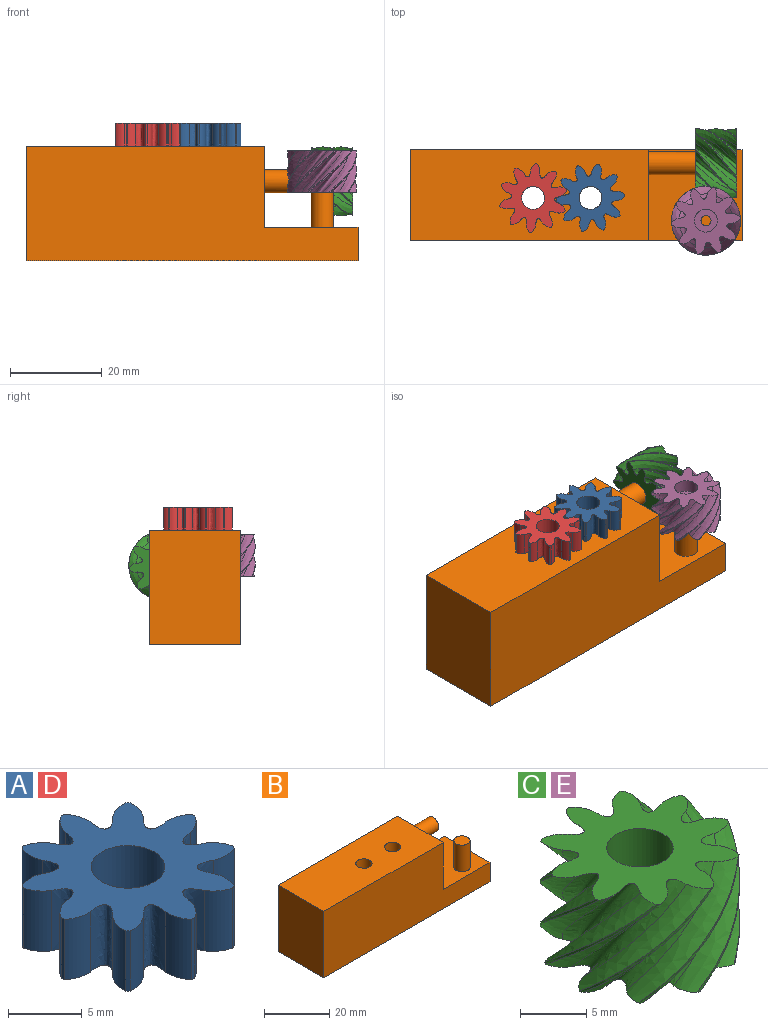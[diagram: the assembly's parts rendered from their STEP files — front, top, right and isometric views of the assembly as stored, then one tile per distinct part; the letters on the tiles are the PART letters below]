
ASSEMBLY  parts=5 mates=4
PART A: 43 faces, bbox 14.9x14.9x5 mm
  f0: cylinder r=2.5mm len=5mm, axis (0,0,-1), area 9.9mm2, adj f1,f39,f40,f41
  f1: cylinder r=7.5mm len=5mm, axis (0,0,-1), area 1.6mm2, adj f0,f2,f40,f41
  f2: cylinder r=2.5mm len=5mm, axis (0,0,-1), area 9.9mm2, adj f1,f3,f40,f41
  f3: extruded ~5x1.49mm, area 14.6mm2, adj f2,f4,f40,f41
  f4: cylinder r=2.5mm len=5mm, axis (0,0,-1), area 9.9mm2, adj f3,f5,f40,f41
  f5: cylinder r=7.5mm len=5mm, axis (0,0,-1), area 1.6mm2, adj f4,f6,f40,f41
  f6: cylinder r=2.5mm len=5mm, axis (0,0,-1), area 9.9mm2, adj f5,f7,f40,f41
  f7: extruded ~5x1.49mm, area 14.6mm2, adj f6,f8,f40,f41
  f8: cylinder r=2.5mm len=5mm, axis (0,0,-1), area 9.9mm2, adj f7,f9,f40,f41
  f9: cylinder r=7.5mm len=5mm, axis (0,0,-1), area 1.6mm2, adj f8,f10,f40,f41
  f10: cylinder r=2.5mm len=5mm, axis (0,0,-1), area 9.9mm2, adj f9,f11,f40,f41
  f11: extruded ~5x1.57mm, area 14.6mm2, adj f10,f12,f40,f41
  f12: cylinder r=2.5mm len=5mm, axis (0,0,-1), area 9.9mm2, adj f11,f13,f40,f41
  f13: cylinder r=7.5mm len=5mm, axis (0,0,-1), area 1.6mm2, adj f12,f14,f40,f41
  f14: cylinder r=2.5mm len=5mm, axis (0,0,-1), area 9.9mm2, adj f13,f15,f40,f41
  f15: extruded ~5x1.48mm, area 14.6mm2, adj f14,f16,f40,f41
  f16: cylinder r=2.5mm len=5mm, axis (0,0,-1), area 9.9mm2, adj f15,f17,f40,f41
  f17: cylinder r=7.5mm len=5mm, axis (0,0,-1), area 1.6mm2, adj f16,f18,f40,f41
  f18: cylinder r=2.5mm len=5mm, axis (0,0,-1), area 9.9mm2, adj f17,f19,f40,f41
  f19: extruded ~5x1.57mm, area 14.6mm2, adj f18,f20,f40,f41
  f20: cylinder r=2.5mm len=5mm, axis (0,0,-1), area 9.9mm2, adj f19,f21,f40,f41
  f21: cylinder r=7.5mm len=5mm, axis (0,0,-1), area 1.6mm2, adj f20,f22,f40,f41
  f22: cylinder r=2.5mm len=5mm, axis (0,0,-1), area 9.9mm2, adj f21,f23,f40,f41
  f23: extruded ~5x1.49mm, area 14.6mm2, adj f22,f24,f40,f41
  f24: cylinder r=2.5mm len=5mm, axis (0,0,-1), area 9.9mm2, adj f23,f25,f40,f41
  f25: cylinder r=7.5mm len=5mm, axis (0,0,-1), area 1.6mm2, adj f24,f26,f40,f41
  f26: cylinder r=2.5mm len=5mm, axis (0,0,-1), area 9.9mm2, adj f25,f27,f40,f41
  f27: extruded ~5x1.49mm, area 14.6mm2, adj f26,f28,f40,f41
  f28: cylinder r=2.5mm len=5mm, axis (0,0,-1), area 9.9mm2, adj f27,f29,f40,f41
  f29: cylinder r=7.5mm len=5mm, axis (0,0,-1), area 1.6mm2, adj f28,f30,f40,f41
  f30: cylinder r=2.5mm len=5mm, axis (0,0,-1), area 9.9mm2, adj f29,f31,f40,f41
  f31: extruded ~5x1.57mm, area 14.6mm2, adj f30,f32,f40,f41
  f32: cylinder r=2.5mm len=5mm, axis (0,0,-1), area 9.9mm2, adj f31,f33,f40,f41
  f33: cylinder r=7.5mm len=5mm, axis (0,0,-1), area 1.6mm2, adj f32,f34,f40,f41
  f34: cylinder r=2.5mm len=5mm, axis (0,0,-1), area 9.9mm2, adj f33,f35,f40,f41
  f35: extruded ~5x1.48mm, area 14.6mm2, adj f34,f36,f40,f41
  f36: cylinder r=2.5mm len=5mm, axis (0,0,-1), area 9.9mm2, adj f35,f37,f40,f41
  f37: cylinder r=7.5mm len=5mm, axis (0,0,-1), area 1.6mm2, adj f36,f38,f40,f41
  f38: cylinder r=2.5mm len=5mm, axis (0,0,-1), area 9.9mm2, adj f37,f39,f40,f41
  f39: extruded ~5x1.57mm, area 14.6mm2, adj f0,f38,f40,f41
  f40: plane 14.86x14.86mm, normal (0,0,1), area 100mm2, adj f0,f1,f2,f3,f4,f5,f6,f7
  f41: plane 14.86x14.86mm, normal (0,0,-1), area 100mm2, adj f0,f1,f2,f3,f4,f5,f6,f7
  f42: cylinder r=2.5mm len=5mm, axis (0,0,1), area 78.5mm2, adj f40,f41
PART B: 14 faces, bbox 72.3x19.9x25 mm
  f0: plane 19.87x7.31mm, normal (1,0,0), area 145.3mm2, adj f1,f3,f7,f8
  f1: plane 72.29x25mm, normal (0,1,0), area 1447.5mm2, adj f0,f2,f6,f7,f8,f9
  f2: plane 25x19.87mm, normal (-1,0,0), area 496.8mm2, adj f1,f3,f6,f7
  f3: plane 72.29x25mm, normal (0,-1,0), area 1447.5mm2, adj f0,f2,f6,f7,f8,f9
  f4: cylinder r=2.5mm len=25mm, axis (0,0,-1), area 392.7mm2, adj f6,f7
  f5: cylinder r=2.5mm len=25mm, axis (0,0,-1), area 392.7mm2, adj f6,f7
  f6: plane 51.95x19.87mm, normal (0,0,1), area 993mm2, adj f1,f2,f3,f4,f5,f9
  f7: plane 72.29x19.87mm, normal (0,0,-1), area 1397.1mm2, adj f0,f1,f2,f3,f4,f5
  f8: plane 20.33x19.87mm, normal (0,0,1), area 384.4mm2, adj f0,f1,f3,f9,f12
  f9: plane 19.87x17.69mm, normal (1,0,0), area 331.8mm2, adj f1,f3,f6,f8,f10
  f10: cylinder r=2.5mm len=12.5mm, axis (-1,0,0), area 196.3mm2, adj f9,f11
  f11: plane 5x5mm, normal (1,0,0), area 19.6mm2, adj f10
  f12: cylinder r=2.5mm len=10mm, axis (0,0,-1), area 157.1mm2, adj f8,f13
  f13: plane 5x5mm, normal (0,0,1), area 19.6mm2, adj f12
PART C: 47 faces, bbox 15.3x15.3x9.1 mm
  f0: cylinder r=2.5mm len=5mm, axis (0,0,-1), area 44mm2, adj f1,f45
  f1: plane 14.96x14.96mm, normal (0,0,-1), area 100mm2, adj f0,f3,f4,f5,f6,f7,f8,f9
  f2: plane 15.15x14.62mm, normal (0,0,1), area 100mm2, adj f3,f4,f5,f6,f7,f8,f9,f10
  f3: bspline ~9x7.62mm, area 23.7mm2, adj f1,f2,f4,f42
  f4: bspline ~9x7.78mm, area 2.8mm2, adj f1,f2,f3,f5
  f5: bspline ~9x8.57mm, area 23.7mm2, adj f1,f2,f4,f6
  f6: bspline ~9x8.24mm, area 32.2mm2, adj f1,f2,f5,f7
  f7: bspline ~9.88x9mm, area 23.7mm2, adj f1,f2,f6,f8
  f8: bspline ~10.1x9mm, area 2.8mm2, adj f1,f2,f7,f9
  f9: bspline ~9.96x9mm, area 23.7mm2, adj f1,f2,f8,f10
  f10: bspline ~9x8.6mm, area 32.2mm2, adj f1,f2,f9,f11
  f11: bspline ~9.1x9mm, area 23.7mm2, adj f1,f2,f10,f12
  f12: bspline ~9x8.56mm, area 2.8mm2, adj f1,f2,f11,f13
  f13: bspline ~9x8.25mm, area 23.7mm2, adj f1,f2,f12,f14
  f14: bspline ~9x6.82mm, area 32.2mm2, adj f1,f2,f13,f15
  f15: bspline ~9.11x9mm, area 23.7mm2, adj f1,f2,f14,f16
  f16: bspline ~9.4x9mm, area 2.8mm2, adj f1,f2,f15,f17
  f17: bspline ~9.63x9mm, area 23.7mm2, adj f1,f2,f16,f18
  f18: bspline ~9x8.85mm, area 32.2mm2, adj f1,f2,f17,f19
  f19: bspline ~9.83x9mm, area 23.7mm2, adj f1,f2,f18,f20
  f20: bspline ~9.81x9mm, area 2.8mm2, adj f1,f2,f19,f21
  f21: bspline ~9.53x9mm, area 23.7mm2, adj f1,f2,f20,f22
  f22: bspline ~9x7.5mm, area 32.2mm2, adj f1,f2,f21,f23
  f23: bspline ~9x7.62mm, area 23.7mm2, adj f1,f2,f22,f24
  f24: bspline ~9x7.78mm, area 2.8mm2, adj f1,f2,f23,f25
  f25: bspline ~9x8.57mm, area 23.7mm2, adj f1,f2,f24,f26
  f26: bspline ~9x8.24mm, area 32.2mm2, adj f1,f2,f25,f27
  f27: bspline ~9.88x9mm, area 23.7mm2, adj f1,f2,f26,f28
  f28: bspline ~10.1x9mm, area 2.8mm2, adj f1,f2,f27,f29
  f29: bspline ~9.96x9mm, area 23.7mm2, adj f1,f2,f28,f30
  f30: bspline ~9x8.6mm, area 32.2mm2, adj f1,f2,f29,f31
  f31: bspline ~9.1x9mm, area 23.7mm2, adj f1,f2,f30,f32
  f32: bspline ~9x8.56mm, area 2.8mm2, adj f1,f2,f31,f33
  f33: bspline ~9x8.25mm, area 23.7mm2, adj f1,f2,f32,f34
  f34: bspline ~9x6.82mm, area 32.2mm2, adj f1,f2,f33,f35
  f35: bspline ~9.11x9mm, area 23.7mm2, adj f1,f2,f34,f36
  f36: bspline ~9.4x9mm, area 2.8mm2, adj f1,f2,f35,f37
  f37: bspline ~9.63x9mm, area 23.7mm2, adj f1,f2,f36,f38
  f38: bspline ~9x8.85mm, area 32.2mm2, adj f1,f2,f37,f39
  f39: bspline ~9.83x9mm, area 23.7mm2, adj f1,f2,f38,f40
  f40: bspline ~9.81x9mm, area 2.8mm2, adj f1,f2,f39,f41
  f41: bspline ~9.53x9mm, area 23.7mm2, adj f1,f2,f40,f42
  f42: bspline ~9x7.5mm, area 32.2mm2, adj f1,f2,f3,f41
  f43: cylinder r=2.5mm len=5mm, axis (0,0,-1), area 73.8mm2, adj f2,f44
  f44: plane 5x5mm, normal (0,0,1), area 15.8mm2, adj f43,f46
  f45: plane 5x5mm, normal (0,0,-1), area 15.8mm2, adj f0,f46
  f46: cylinder r=1.1mm len=2.2mm, axis (0,0,-1), area 10.4mm2, adj f44,f45
PART D: same geometry as A
PART E: same geometry as C
PLACE A rot(axis=(0,0,-1),40.5deg) t=(6.25,0,25)mm
PLACE B at identity fixed
PLACE C rot(axis=(-0.52,-0.67,0.52),112.3deg) t=(38.05,7.56,17.31)mm
PLACE D rot(axis=(0,0,1),40.5deg) t=(-6.25,0,25)mm
PLACE E rot(axis=(-0.99,-0.12,0),180deg) t=(31.4,-4.94,23.96)mm
MATE revolute E.f0 <-> B.f12  axis (0,0,1) through (31.4,-4.94,17.31)mm
MATE revolute C.f0 <-> B.f10  axis (1,0,0) through (31.4,7.56,17.31)mm
MATE revolute D.f42 <-> B.f4  axis (0,0,1) through (-6.25,0,25)mm
MATE revolute B.f5 <-> A.f42  axis (0,0,1) through (6.25,0,25)mm
